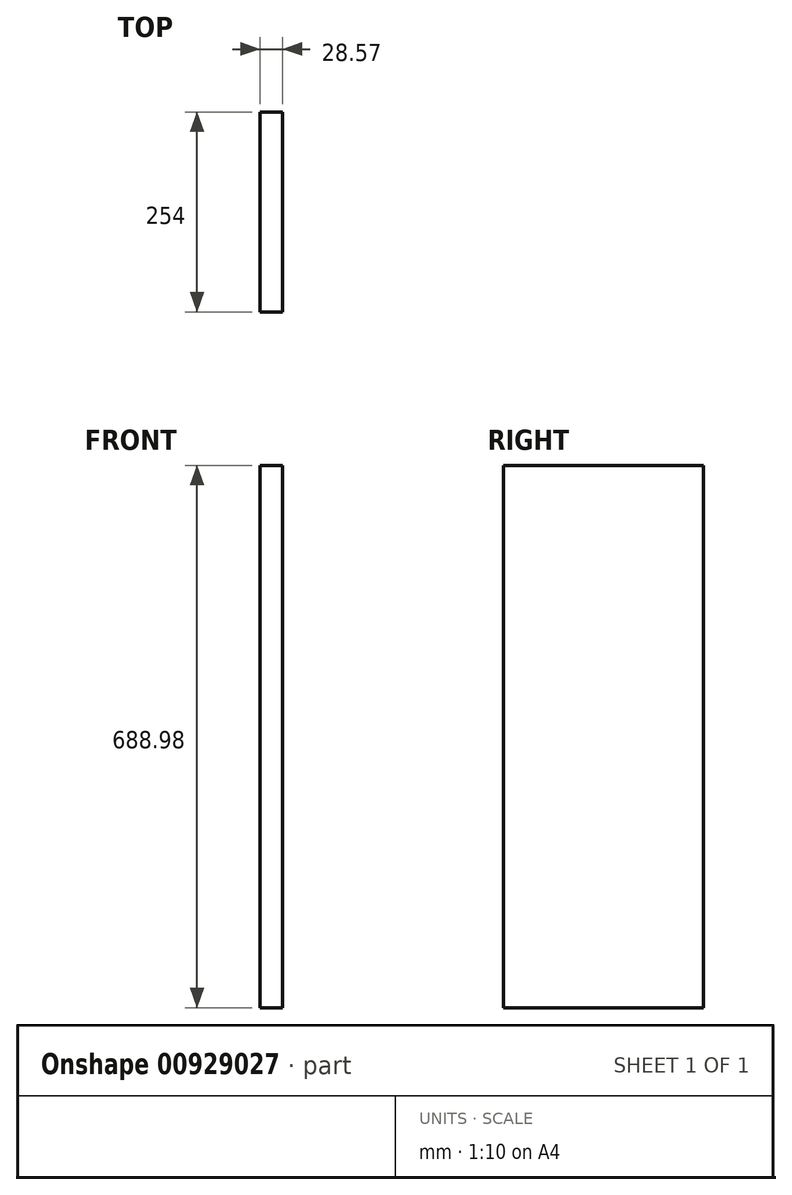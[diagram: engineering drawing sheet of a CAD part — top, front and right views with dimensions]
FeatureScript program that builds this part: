
annotation { "Feature Type Name" : "Feature", "Feature Type Description" : "" }
export const myFeature = defineFeature(function(context is Context, id is Id, definition is map)
    precondition{}
    {
        {
            var Q0;
            Q0=qCreatedBy(makeId("Right.planeOp"),FACE);
            var sketch = newSketch(context, id + "F0", { "sketchPlane" : qUnion([Q0])});
            skLineSegment(sketch, "E0.bottom", {"start": v(127, 344.49) * mm, "end": v(-127, 344.49) * mm});
            skLineSegment(sketch, "E0.top", {"start": v(127, -344.49) * mm, "end": v(-127, -344.49) * mm});
            skLineSegment(sketch, "E0.left", {"start": v(127, 344.49) * mm, "end": v(127, -344.49) * mm});
            skLineSegment(sketch, "E0.right", {"start": v(-127, 344.49) * mm, "end": v(-127, -344.49) * mm});
            skPoint(sketch, "E0.middle", {"position": v(0, 0) * mm});
            skSolve(sketch);
        }
        {
            var Q0;
            Q0=makeQuery(id+"F0.imprint","IMPRINT",FACE,{"disambiguationData":[TD([[makeQuery(id+"F0.imprint","IMPRINT",EDGE,{"derivedFrom":sQuery(id+"F0.wireOp",EDGE,"E0.bottom")}),1.0]])]});
            extrude(context, id + "F1", {"entities" : qUnion([Q0]), "depth" : 28.57 * mm, "offsetDistance" : 25.4 * mm});
        }
    });
